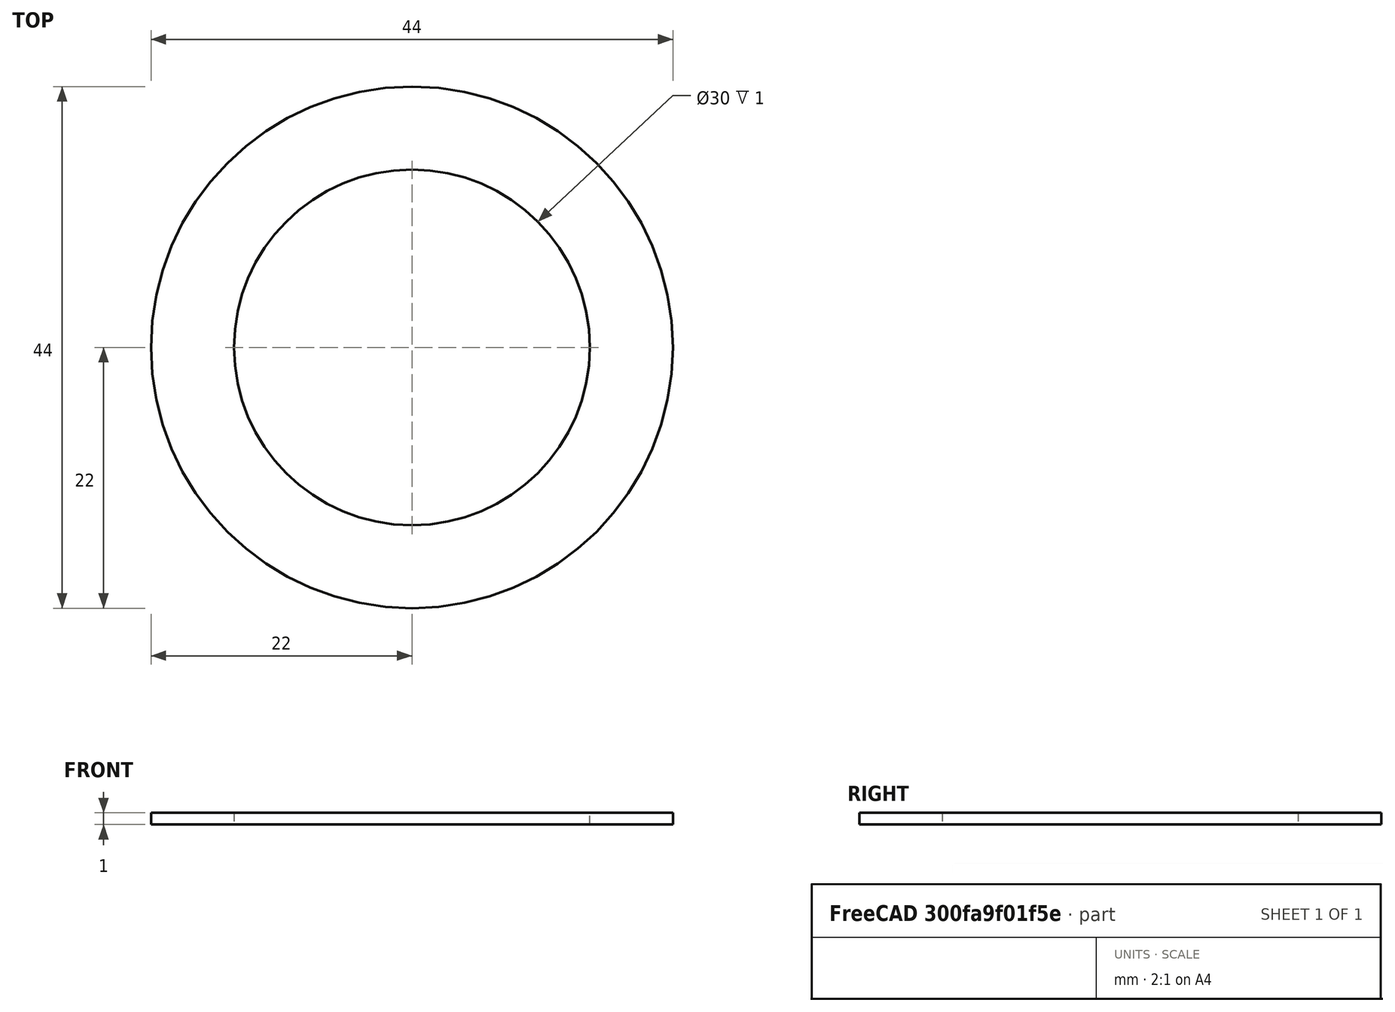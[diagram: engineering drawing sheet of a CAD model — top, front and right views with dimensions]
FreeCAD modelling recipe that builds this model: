
FCSTD DOCUMENT  (FreeCAD 1.0R38641 +678 (Git))
Label: volvo_gear_selector_spacer
License: All rights reserved
LicenseURL: https://en.wikipedia.org/wiki/All_rights_reserved
objects: Sketcher::SketchObject×1, PartDesign::Pad×1, PartDesign::Body×1
note: 6 computed .brp shape members not serialized (recipe doc carries the construction recipe); baked Part::Feature solids carry a one-line shape summary decoded from their .brp

FEATURE [Sketcher::SketchObject] Sketch
  ArcFitTolerance = 1e-06
  AttachmentSupport = -> [XY_Plane]
  FullyConstrained = true
  MakeInternals = false
  MapMode = 5
  sketch-geometry (2):
    g0: Circle CenterX=0 CenterY=0 CenterZ=0 NormalX=0 NormalY=0 NormalZ=1 AngleXU=0 Radius=15
    g1: Circle CenterX=0 CenterY=0 CenterZ=0 NormalX=0 NormalY=0 NormalZ=1 AngleXU=0 Radius=22
  constraints (4):
    c: Coincident(g0,g-1)
    c: Coincident(g1,g0)
    c: Diameter(g0) = 30
    c: Diameter(g1) = 44
FEATURE [PartDesign::Pad] Pad
  Direction = (0,0,1)
  Length = 1
  Length2 = 10
  Profile = -> Sketch
  ReferenceAxis = -> Sketch [N_Axis]
  Refine = true
  Suppressed = false
  Type = 0
FEATURE [PartDesign::Body] Body
  AllowCompound = false
  Group = -> [Sketch,Pad]
  Origin = -> Origin
  Tip = -> Pad
